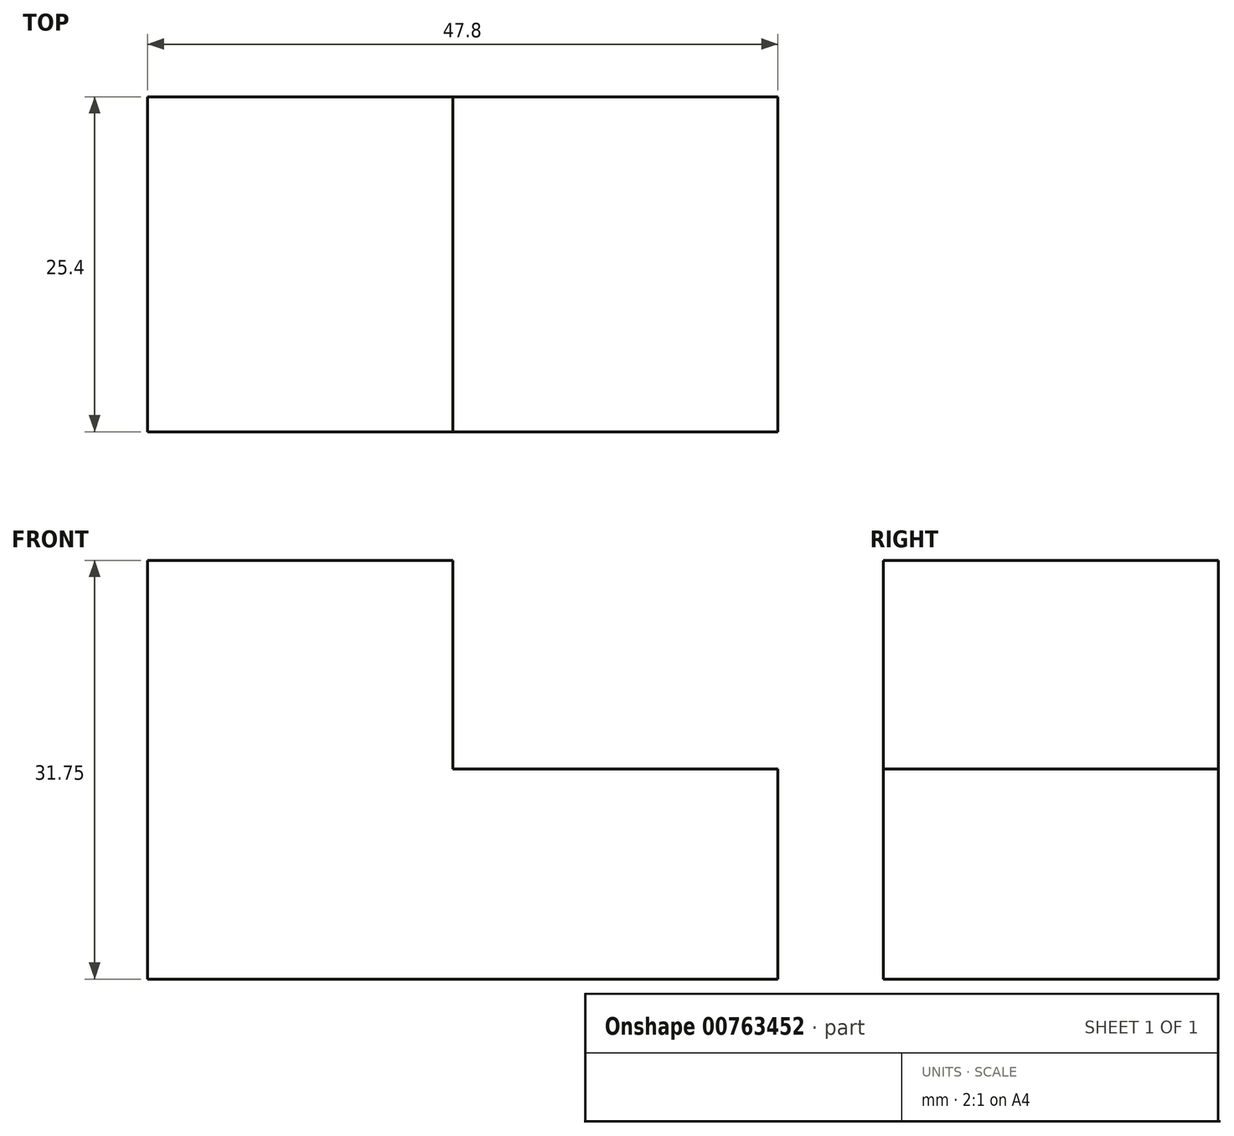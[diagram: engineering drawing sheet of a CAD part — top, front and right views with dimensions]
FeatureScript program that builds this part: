
annotation { "Feature Type Name" : "Feature", "Feature Type Description" : "" }
export const myFeature = defineFeature(function(context is Context, id is Id, definition is map)
    precondition{}
    {
        {
            var Q0;
            Q0=qCreatedBy(makeId("Front.planeOp"),FACE);
            var sketch = newSketch(context, id + "F0", { "sketchPlane" : qUnion([Q0])});
            skLineSegment(sketch, "E0", {"start": v(0, 0) * mm, "end": v(47.8, 0) * mm});
            skLineSegment(sketch, "E1", {"start": v(47.8, 0) * mm, "end": v(47.8, 15.93) * mm});
            skLineSegment(sketch, "E2", {"start": v(47.8, 15.93) * mm, "end": v(23.15, 15.93) * mm});
            skLineSegment(sketch, "E3", {"start": v(23.15, 15.93) * mm, "end": v(23.15, 31.75) * mm});
            skLineSegment(sketch, "E4", {"start": v(23.15, 31.75) * mm, "end": v(0, 31.75) * mm});
            skLineSegment(sketch, "E5", {"start": v(0, 0) * mm, "end": v(0, 31.75) * mm});
            skSolve(sketch);
        }
        {
            var Q0;
            Q0=makeQuery(id+"F0.imprint","IMPRINT",FACE,{"disambiguationData":[TD([[makeQuery(id+"F0.imprint","IMPRINT",EDGE,{"derivedFrom":sQuery(id+"F0.wireOp",EDGE,"E0")}),1.0]])]});
            extrude(context, id + "F1", {"entities" : qUnion([Q0]), "depth" : 25.4 * mm, "offsetDistance" : 25.4 * mm});
        }
    });
